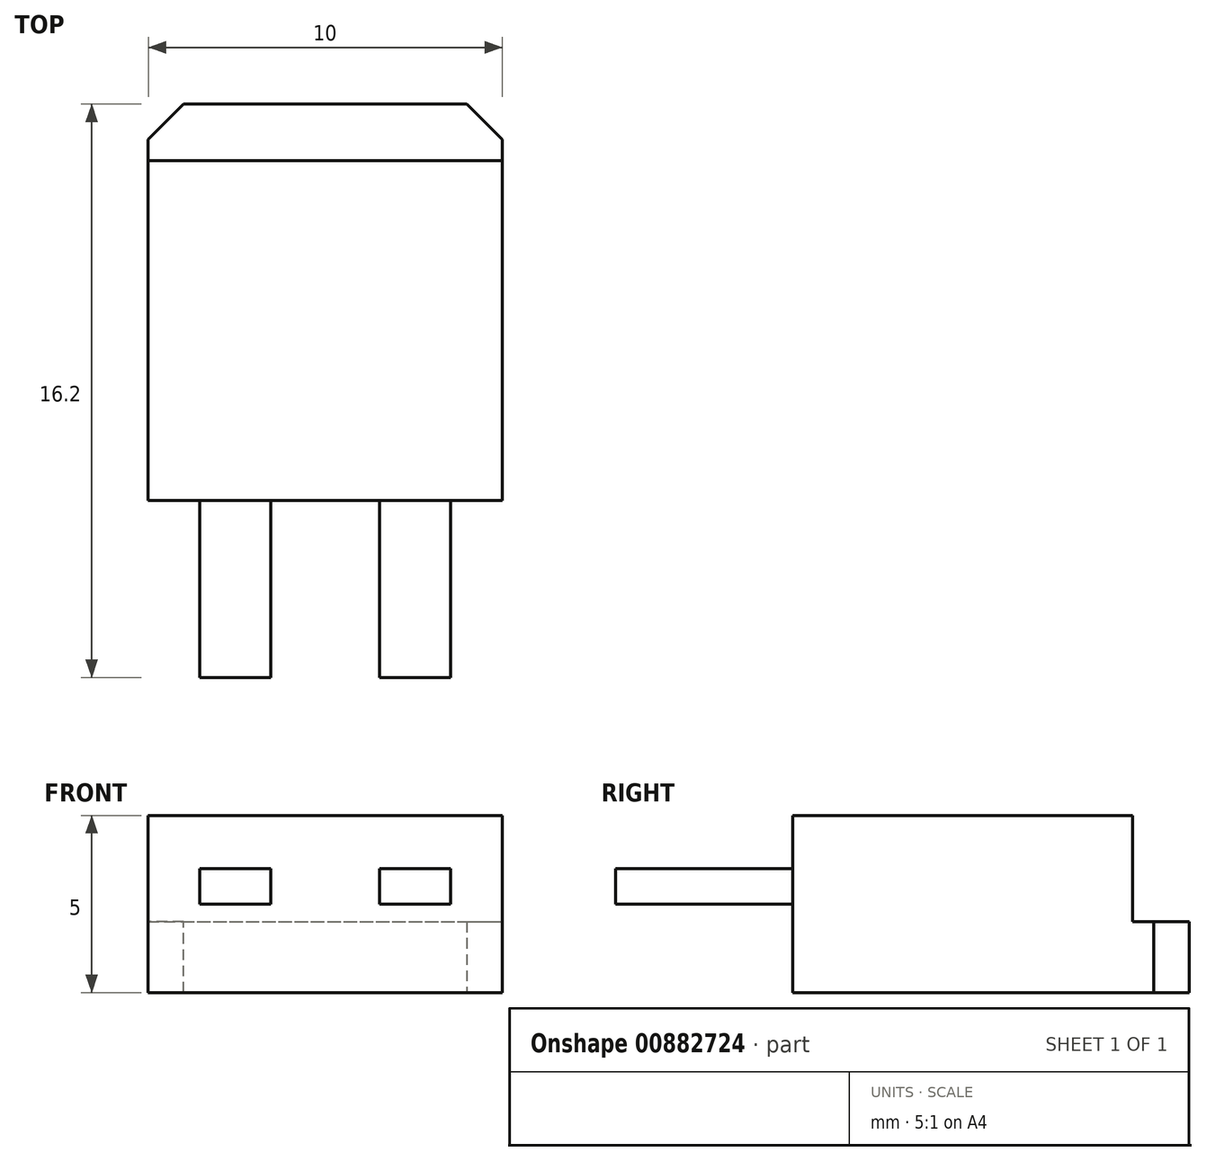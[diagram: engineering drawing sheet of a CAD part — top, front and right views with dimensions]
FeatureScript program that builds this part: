
annotation { "Feature Type Name" : "Feature", "Feature Type Description" : "" }
export const myFeature = defineFeature(function(context is Context, id is Id, definition is map)
    precondition{}
    {
        {
            var Q0;
            Q0=qCreatedBy(makeId("Top.planeOp"),FACE);
            var sketch = newSketch(context, id + "F0", { "sketchPlane" : qUnion([Q0])});
            skLineSegment(sketch, "E0.bottom", {"start": v(-2.83, 5.35) * mm, "end": v(7.17, 5.35) * mm});
            skLineSegment(sketch, "E0.top", {"start": v(-2.83, -5.85) * mm, "end": v(7.17, -5.85) * mm});
            skLineSegment(sketch, "E0.left", {"start": v(-2.83, 5.35) * mm, "end": v(-2.83, -5.85) * mm});
            skLineSegment(sketch, "E0.right", {"start": v(7.17, 5.35) * mm, "end": v(7.17, -5.85) * mm});
            skSolve(sketch);
        }
        {
            var Q0;
            Q0=makeQuery(id+"F0.imprint","IMPRINT",FACE,{"disambiguationData":[TD([[makeQuery(id+"F0.imprint","IMPRINT",EDGE,{"derivedFrom":sQuery(id+"F0.wireOp",EDGE,"E0.bottom")}),-1.0]])]});
            extrude(context, id + "F1", {"entities" : qUnion([Q0]), "depth" : 5 * mm, "offsetDistance" : 25 * mm});
        }
        {
            var Q0;
            Q0=makeQuery(id+"F1.opExtrude","CAP_FACE",FACE,{"disambiguationData":[OSD([sQuery(id+"F0.wireOp",EDGE,"E0.bottom"),sQuery(id+"F0.wireOp",EDGE,"E0.top"),sQuery(id+"F0.wireOp",EDGE,"E0.left"),sQuery(id+"F0.wireOp",EDGE,"E0.right")])],"isStart":false});
            var sketch = newSketch(context, id + "F2", { "sketchPlane" : qUnion([Q0])});
            skLineSegment(sketch, "E1.bottom", {"start": v(-2.83, 5.35) * mm, "end": v(7.17, 5.35) * mm});
            skLineSegment(sketch, "E1.top", {"start": v(-2.83, 3.75) * mm, "end": v(7.17, 3.75) * mm});
            skLineSegment(sketch, "E1.left", {"start": v(-2.83, 5.35) * mm, "end": v(-2.83, 3.75) * mm});
            skLineSegment(sketch, "E1.right", {"start": v(7.17, 5.35) * mm, "end": v(7.17, 3.75) * mm});
            skSolve(sketch);
        }
        {
            var Q0;
            Q0=makeQuery(id+"F2.imprint","IMPRINT",FACE,{"disambiguationData":[TD([[makeQuery(id+"F2.imprint","IMPRINT",EDGE,{"derivedFrom":sQuery(id+"F2.wireOp",EDGE,"E1.bottom")}),-1.0]])]});
            extrude(context, id + "F3", {"entities" : qUnion([Q0]), "operationType" : NewBodyOperationType.REMOVE, "oppositeDirection" : true, "depth" : 3 * mm, "offsetDistance" : 25 * mm});
        }
        {
            var Q0;
            Q0=makeQuery(id+"F1.opExtrude","SWEPT_EDGE",EDGE,{"disambiguationData":[OSD([sQuery(id+"F0.wireOp",EDGE,"E0.bottom"),sQuery(id+"F0.wireOp",EDGE,"E0.right")])]});
            var Q1;
            Q1=makeQuery(id+"F1.opExtrude","SWEPT_EDGE",EDGE,{"disambiguationData":[OSD([sQuery(id+"F0.wireOp",EDGE,"E0.bottom"),sQuery(id+"F0.wireOp",EDGE,"E0.left")])]});
            chamfer(context, id + "F4", {"entities" : qUnion([Q0, Q1]), "width" : 1 * mm, "tangentPropagation" : true});
        }
        {
            var Q0;
            Q0=makeQuery(id+"F1.opExtrude","SWEPT_FACE",FACE,{"disambiguationData":[OSD([sQuery(id+"F0.wireOp",EDGE,"E0.top")])]});
            var sketch = newSketch(context, id + "F5", { "sketchPlane" : qUnion([Q0])});
            skLineSegment(sketch, "E2.bottom", {"start": v(-1.37, 3.5) * mm, "end": v(0.63, 3.5) * mm});
            skLineSegment(sketch, "E2.top", {"start": v(-1.37, 2.5) * mm, "end": v(0.63, 2.5) * mm});
            skLineSegment(sketch, "E2.left", {"start": v(-1.37, 3.5) * mm, "end": v(-1.37, 2.5) * mm});
            skLineSegment(sketch, "E2.right", {"start": v(0.63, 3.5) * mm, "end": v(0.63, 2.5) * mm});
            skLineSegment(sketch, "E3", {"start": v(2.17, 5) * mm, "end": v(2.17, 0) * mm, "construction": true});
            skPoint(sketch, "E4", {"position": v(-0.37, 2.5) * mm});
            skLineSegment(sketch, "E5.MirrorCS", {"start": v(3.7, 3.5) * mm, "end": v(3.7, 2.5) * mm});
            skPoint(sketch, "E6.MirrorP", {"position": v(4.7, 2.5) * mm});
            skLineSegment(sketch, "E7.MirrorCS", {"start": v(5.7, 3.5) * mm, "end": v(3.7, 3.5) * mm});
            skLineSegment(sketch, "E8.MirrorCS", {"start": v(5.7, 3.5) * mm, "end": v(5.7, 2.5) * mm});
            skLineSegment(sketch, "E9.MirrorCS", {"start": v(5.7, 2.5) * mm, "end": v(3.7, 2.5) * mm});
            skSolve(sketch);
        }
        {
            var Q0;
            Q0=makeQuery(id+"F5.imprint","IMPRINT",FACE,{"disambiguationData":[TD([[makeQuery(id+"F5.imprint","IMPRINT",EDGE,{"derivedFrom":sQuery(id+"F5.wireOp",EDGE,"E2.bottom")}),-1.0]])]});
            var Q1;
            Q1=makeQuery(id+"F5.imprint","IMPRINT",FACE,{"disambiguationData":[TD([[makeQuery(id+"F5.imprint","IMPRINT",EDGE,{"derivedFrom":sQuery(id+"F5.wireOp",EDGE,"E5.MirrorCS")}),1.0]])]});
            extrude(context, id + "F6", {"entities" : qUnion([Q0, Q1]), "operationType" : NewBodyOperationType.ADD, "depth" : 5 * mm, "offsetDistance" : 25 * mm});
        }
    });
